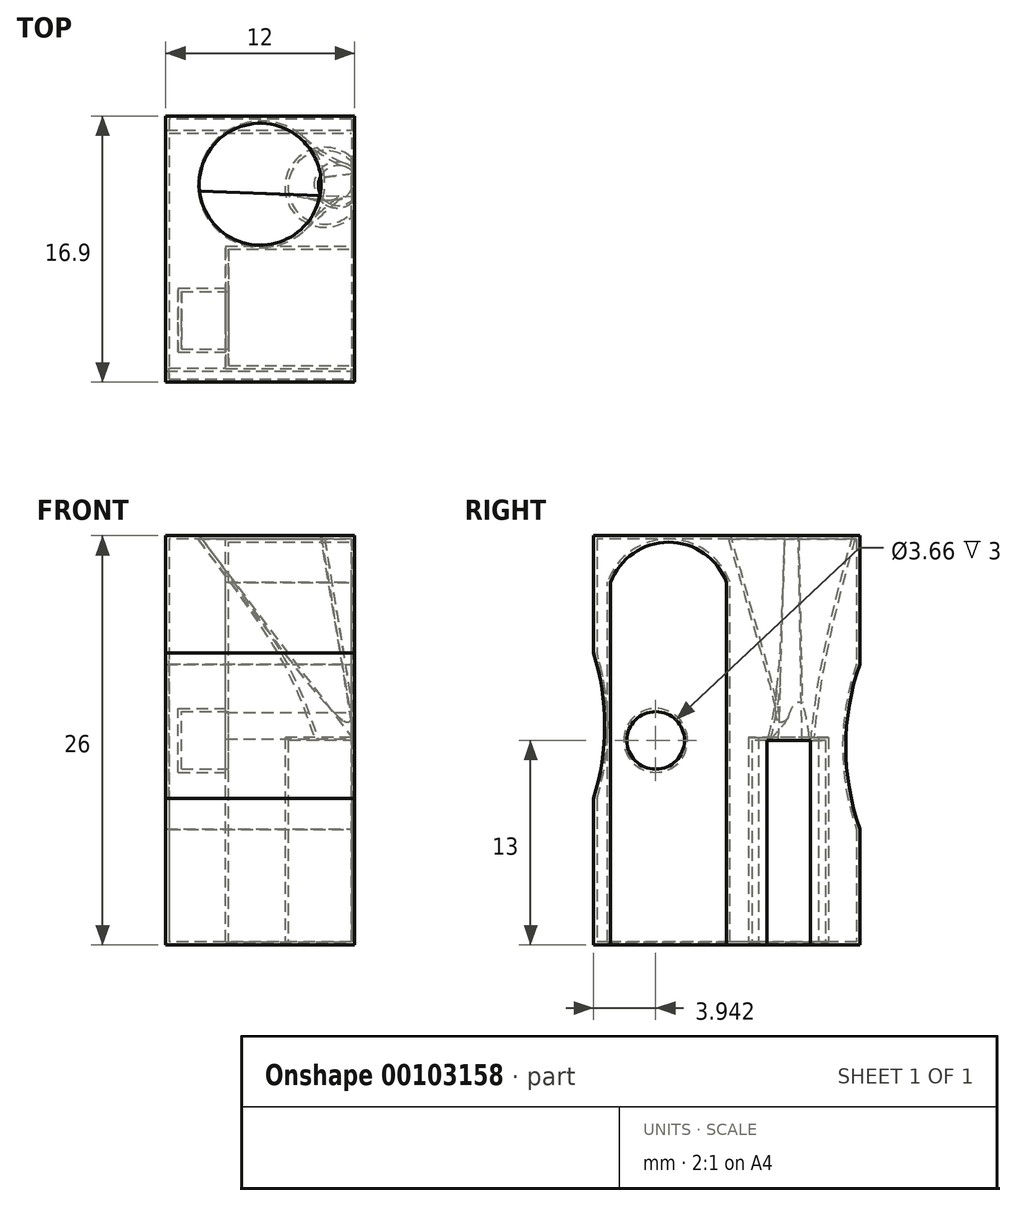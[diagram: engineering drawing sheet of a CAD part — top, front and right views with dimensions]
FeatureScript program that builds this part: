
annotation { "Feature Type Name" : "Feature", "Feature Type Description" : "" }
export const myFeature = defineFeature(function(context is Context, id is Id, definition is map)
    precondition{}
    {
        {
            var Q0;
            Q0=qCreatedBy(makeId("Right.planeOp"),FACE);
            var sketch = newSketch(context, id + "F0", { "sketchPlane" : qUnion([Q0])});
            skLineSegment(sketch, "E0.bottom", {"start": v(8.45, 13) * mm, "end": v(-8.45, 13) * mm});
            skLineSegment(sketch, "E0.top", {"start": v(8.45, -13) * mm, "end": v(-8.45, -13) * mm});
            skLineSegment(sketch, "E0.left", {"start": v(8.45, 13) * mm, "end": v(8.45, -13) * mm});
            skLineSegment(sketch, "E0.right", {"start": v(-8.45, 13) * mm, "end": v(-8.45, -13) * mm});
            skPoint(sketch, "E0.middle", {"position": v(0, 0) * mm});
            skSolve(sketch);
        }
        {
            var Q0;
            Q0 = qSketchRegion(id + "F0", true);
            extrude(context, id + "F1", {"entities" : qUnion([Q0]), "endBound" : BoundingType.SYMMETRIC, "depth" : 12 * mm});
        }
        {
            var Q0;
            Q0=qCreatedBy(makeId("Right.planeOp"),FACE);
            cPlane(context, id + "F2", {"entities" : qUnion([Q0]), "cplaneType" : CPlaneType.OFFSET, "offset" : 6 * mm, "width" : 150 * mm, "height" : 150 * mm});
        }
        {
            var Q0;
            Q0=qCreatedBy(id+"F2.planeOp",FACE);
            var sketch = newSketch(context, id + "F3", { "sketchPlane" : qUnion([Q0])});
            skLineSegment(sketch, "E1", {"start": v(0, 0) * mm, "end": v(0, 10.03) * mm});
            skLineSegment(sketch, "E2", {"start": v(-7.38, 0) * mm, "end": v(-7.38, 10.03) * mm});
            skLineSegment(sketch, "E3", {"start": v(-7.38, 0) * mm, "end": v(-7.38, -13) * mm});
            skLineSegment(sketch, "E4", {"start": v(0, 0) * mm, "end": v(0, -13) * mm});
            skArc(sketch, "E5", {"start": v(0, 10.03) * mm, "mid": v(-3.69, 12.59) * mm, "end": v(-7.38, 10.03) * mm});
            skLineSegment(sketch, "E6", {"start": v(-7.38, -13) * mm, "end": v(0, -13) * mm});
            skSolve(sketch);
        }
        {
            var Q0;
            Q0 = qSketchRegion(id + "F3", true);
            extrude(context, id + "F4", {"entities" : qUnion([Q0]), "operationType" : NewBodyOperationType.REMOVE, "oppositeDirection" : true, "depth" : 8 * mm});
        }
        {
            var Q0;
            Q0=qCreatedBy(makeId("Top.planeOp"),FACE);
            cPlane(context, id + "F5", {"entities" : qUnion([Q0]), "cplaneType" : CPlaneType.OFFSET, "offset" : 13 * mm, "width" : 150 * mm, "height" : 150 * mm});
        }
        {
            var Q0;
            Q0=qCreatedBy(makeId("Top.planeOp"),FACE);
            cPlane(context, id + "F6", {"entities" : qUnion([Q0]), "cplaneType" : CPlaneType.OFFSET, "offset" : 13 * mm, "oppositeDirection" : true, "width" : 150 * mm, "height" : 150 * mm});
        }
        {
            var Q0;
            Q0=qCreatedBy(id+"F6.planeOp",FACE);
            var sketch = newSketch(context, id + "F7", { "sketchPlane" : qUnion([Q0])});
            skArc(sketch, "E7", {"start": v(6, 5.31) * mm, "mid": v(1.77, 3.93) * mm, "end": v(6, 2.55) * mm});
            skLineSegment(sketch, "E8", {"start": v(6, 2.55) * mm, "end": v(6, 5.31) * mm});
            skSolve(sketch);
        }
        {
            var Q0;
            Q0=qCreatedBy(id+"F5.planeOp",FACE);
            var sketch = newSketch(context, id + "F8", { "sketchPlane" : qUnion([Q0])});
            skCircle(sketch, "E9", {"center": v(0, 4.13) * mm, "radius": 3.87 * mm});
            skSolve(sketch);
        }
        {
            var Q0;
            Q0 = qSketchRegion(id + "F7", true);
            extrude(context, id + "F9", {"entities" : qUnion([Q0]), "operationType" : NewBodyOperationType.REMOVE, "depth" : 13 * mm});
        }
        {
            var Q0;
            Q0=qCreatedBy(makeId("Top.planeOp"),FACE);
            var sketch = newSketch(context, id + "F10", { "sketchPlane" : qUnion([Q0])});
            skArc(sketch, "E10", {"start": v(6, 4.79) * mm, "mid": v(3.7, 4.04) * mm, "end": v(6, 3.3) * mm});
            skLineSegment(sketch, "E11", {"start": v(6, 3.3) * mm, "end": v(6, 4.79) * mm});
            skSolve(sketch);
        }
        {
            var Q1;
            Q1 = qSketchRegion(id + "F10", true);
            var Q2;
            Q2 = qSketchRegion(id + "F8", true);
            loft(context, id + "F11", {"operationType" : NewBodyOperationType.REMOVE, "sheetProfilesArray" : [{ "sheetProfileEntities" : qUnion([Q1]) }, { "sheetProfileEntities" : qUnion([Q2]) }]});
        }
        {
            var Q0;
            Q0=qCreatedBy(id+"F2.planeOp",FACE);
            cPlane(context, id + "F12", {"entities" : qUnion([Q0]), "cplaneType" : CPlaneType.OFFSET, "offset" : 8 * mm, "oppositeDirection" : true, "width" : 150 * mm, "height" : 150 * mm});
        }
        {
            var Q0;
            Q0=qCreatedBy(id+"F12.planeOp",FACE);
            var sketch = newSketch(context, id + "F13", { "sketchPlane" : qUnion([Q0])});
            skCircle(sketch, "E12", {"center": v(-4.5, 0) * mm, "radius": 1.83 * mm});
            skSolve(sketch);
        }
        {
            var Q0;
            Q0 = qSketchRegion(id + "F13", true);
            extrude(context, id + "F14", {"entities" : qUnion([Q0]), "operationType" : NewBodyOperationType.REMOVE, "oppositeDirection" : true, "depth" : 3 * mm});
        }
        {
            var Q0;
            Q0=qCreatedBy(id+"F2.planeOp",FACE);
            var sketch = newSketch(context, id + "F15", { "sketchPlane" : qUnion([Q0])});
            skArc(sketch, "E13", {"start": v(8.45, 4.82) * mm, "mid": v(7.56, -0.4) * mm, "end": v(8.45, -5.61) * mm});
            skLineSegment(sketch, "E14", {"start": v(8.45, 4.82) * mm, "end": v(8.45, -5.61) * mm});
            skArc(sketch, "E15", {"start": v(-8.45, -3.68) * mm, "mid": v(-7.75, 0.94) * mm, "end": v(-8.45, 5.56) * mm});
            skLineSegment(sketch, "E16", {"start": v(-8.45, 5.56) * mm, "end": v(-8.45, -3.68) * mm});
            skSolve(sketch);
        }
        {
            var Q0;
            Q0 = qSketchRegion(id + "F15", true);
            extrude(context, id + "F16", {"entities" : qUnion([Q0]), "operationType" : NewBodyOperationType.REMOVE, "oppositeDirection" : true, "depth" : 12 * mm});
        }
        {
            var Q0;
            Q0=makeQuery(id+"F1.opExtrude","CAP_FACE",FACE,{"disambiguationData":[OSD([sQuery(id+"F0.wireOp",EDGE,"E0.bottom"),sQuery(id+"F0.wireOp",EDGE,"E0.top"),sQuery(id+"F0.wireOp",EDGE,"E0.left"),sQuery(id+"F0.wireOp",EDGE,"E0.right")])],"isStart":true});
            var Q1;
            Q1=makeQuery(id+"F1.opExtrude","SWEPT_BODY",BODY,{"disambiguationData":[OSD([sQuery(id+"F0.wireOp",EDGE,"E0.bottom"),sQuery(id+"F0.wireOp",EDGE,"E0.top"),sQuery(id+"F0.wireOp",EDGE,"E0.left"),sQuery(id+"F0.wireOp",EDGE,"E0.right")])]});
            shell(context, id + "F17", {"isHollow" : true, "entities" : qUnion([Q0]), "parts" : qUnion([Q1]), "thickness" : 0.2 * mm});
        }
    });
